# Revit family: greek-doric-plain-and-fluted-column-bim
name_source: partatom
category: Columns
units: mm (PartAtom-declared; Revit-internal decimal feet)

## family parameters
Automatically joins geometry to walls = Yes
Classification Number = 23.25.30.11.14.11
Cut with Voids When Loaded = No
Shared = No
Show family pre-cut in plan views = Yes

## types (22) — shared parameters
Assembly Code = 066000
Description = Load-bearing or decorative composite column with Tuscan, Doric, or Attic cap/base, available in Cast Fiberglass, Lightweight Fiberglass, Synthetic Stone, or GFRC.
Manufacturer = Royal Corinthian
Model = Greek Doric Fluted & Plain Column
Product Line = RoyalCast / RoyaLite / RoyalStone / RoyalGFRC
URL = https://royalcorinthian.com

## per-type parameters (varying)
| type | Greek Doric Fluted | Greek Doric Plain | Material | Width |
| 14" Greek Doric Fluted Column | Yes | No | RoyalStone Cream | 1' - 2" |
| 16" Greek Doric Fluted Column | Yes | No | RoyalStone Cream | 1' - 4" |
| 21.31" Greek Doric Fluted Column | Yes | No | RoyalStone Cream | 1' - 9 5/16" |
| 22.56" Greek Doric Fluted Column | Yes | No | RoyalStone Cream | 1' - 10 9/16" |
| 23.18" Greek Doric Fluted Column | Yes | No | RoyalStone Cream | 1' - 11 3/16" |
| 23.75" Greek Doric Fluted Column | Yes | No | RoyalStone Cream | 1' - 11 3/4" |
| 24.06" Greek Doric Fluted Column | Yes | No | White | 2' - 0 1/16" |
| 25.18" Greek Doric Fluted Column | Yes | No | RoyalStone Cream | 2' - 1 3/16" |
| 25.81" Greek Doric Fluted Column | Yes | No | RoyalStone Cream | 2' - 1 13/16" |
| 26.37" Greek Doric Fluted Column | Yes | No | RoyalStone Cream | 2' - 2 3/8" |
| 27.25" Greek Doric Fluted Column | Yes | No | RoyalStone Cream | 2' - 3 1/4" |
| 28.18" Greek Doric Fluted Column | Yes | No | RoyalStone Cream | 2' - 4 3/16" |
| 28.56" Greek Doric Fluted Column | Yes | No | RoyalStone Cream | 2' - 4 9/16" |
| 28.87" Greek Doric Fluted Column | Yes | No | RoyalStone Cream | 2' - 4 7/8" |
| 29.56" Greek Doric Fluted Column | Yes | No | RoyalStone Cream | 2' - 5 9/16" |
| 30.18" Greek Doric Fluted Column | Yes | No | RoyalStone Cream | 2' - 6 3/16" |
| 30.87" Greek Doric Fluted Column | Yes | No | RoyalStone Cream | 2' - 6 7/8" |
| 31.56" Greek Doric Fluted Column | Yes | No | RoyalStone Cream | 2' - 7 9/16" |
| 31.87" Greek Doric Fluted Column | Yes | No | RoyalStone Cream | 2' - 7 7/8" |
| 12" Greek Doric Plain Column | No | Yes | RoyalStone Cream | 1' - 0" |
| 14" Greek Doric Plain Column | No | Yes | RoyalStone Cream | 1' - 2" |
| 24" Greek Doric Plain Column | No | Yes | RoyalStone Cream | 2' - 0" |

## geometry (parser evidence)
native form markers: Sweep x36
no freeform markers — native parametric forms only
